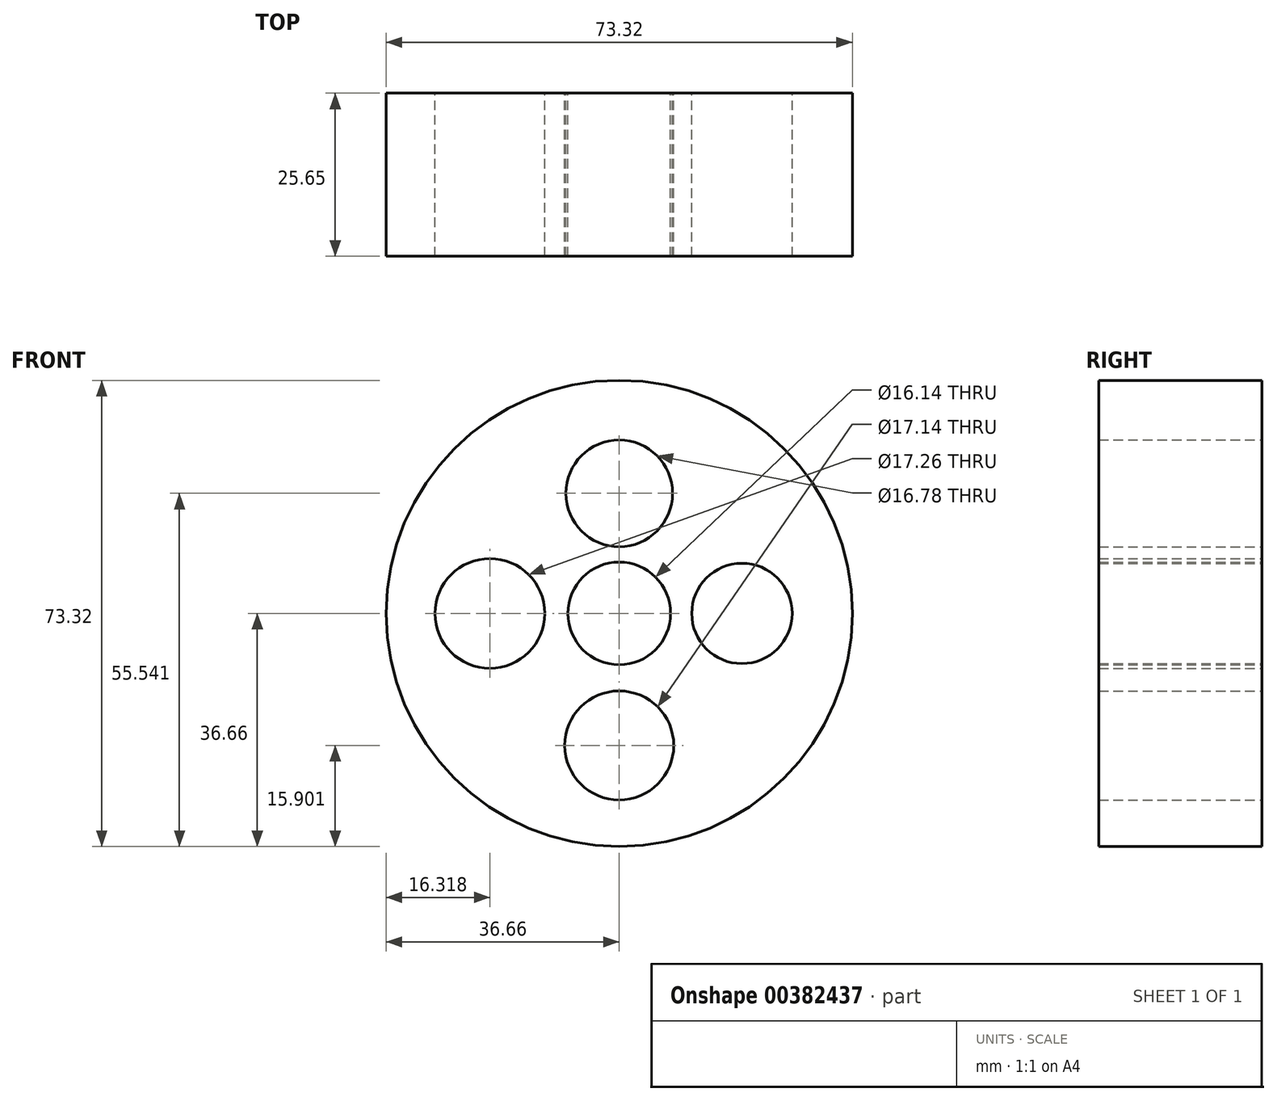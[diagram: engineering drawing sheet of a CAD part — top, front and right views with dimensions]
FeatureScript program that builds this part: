
annotation { "Feature Type Name" : "Feature", "Feature Type Description" : "" }
export const myFeature = defineFeature(function(context is Context, id is Id, definition is map)
    precondition{}
    {
        {
            var Q0;
            Q0=qCreatedBy(makeId("Front.planeOp"),FACE);
            var sketch = newSketch(context, id + "F0", { "sketchPlane" : qUnion([Q0])});
            skCircle(sketch, "E0", {"center": v(0, 0) * mm, "radius": 36.66 * mm});
            skCircle(sketch, "E1", {"center": v(0, 0) * mm, "radius": 32.64 * mm});
            skCircle(sketch, "E2", {"center": v(0, 0) * mm, "radius": 5.84 * mm});
            skCircle(sketch, "E3", {"center": v(0, 0) * mm, "radius": 8.07 * mm});
            skCircle(sketch, "E4", {"center": v(0, -20.76) * mm, "radius": 8.57 * mm});
            skCircle(sketch, "E5", {"center": v(19.3, 0) * mm, "radius": 7.9 * mm});
            skCircle(sketch, "E6", {"center": v(-20.34, 0) * mm, "radius": 8.63 * mm});
            skCircle(sketch, "E7", {"center": v(0, 18.88) * mm, "radius": 8.39 * mm});
            skSolve(sketch);
        }
        {
            var Q0;
            Q0=makeQuery(id+"F0.imprint","IMPRINT",FACE,{"disambiguationData":[TD([[makeQuery(id+"F0.imprint","IMPRINT",EDGE,{"derivedFrom":sQuery(id+"F0.wireOp",EDGE,"E1")}),1.0]])]});
            var Q1;
            Q1=makeQuery(id+"F0.imprint","IMPRINT",FACE,{"disambiguationData":[TD([[makeQuery(id+"F0.imprint","IMPRINT",EDGE,{"derivedFrom":sQuery(id+"F0.wireOp",EDGE,"E0")}),1.0]])]});
            extrude(context, id + "F1", {"entities" : qUnion([Q0, Q1]), "depth" : 25.4 * mm});
        }
        {
            var Q0;
            Q0=makeQuery(id+"F1.opExtrude","CAP_FACE",FACE,{"disambiguationData":[OSD([sQuery(id+"F0.wireOp",EDGE,"E0"),sQuery(id+"F0.wireOp",EDGE,"E3"),sQuery(id+"F0.wireOp",EDGE,"E4"),sQuery(id+"F0.wireOp",EDGE,"E5"),sQuery(id+"F0.wireOp",EDGE,"E6"),sQuery(id+"F0.wireOp",EDGE,"E7")])],"isStart":false});
            extrude(context, id + "F2", {"entities" : qUnion([Q0]), "operationType" : NewBodyOperationType.ADD, "depth" : 0.25 * mm});
        }
    });
